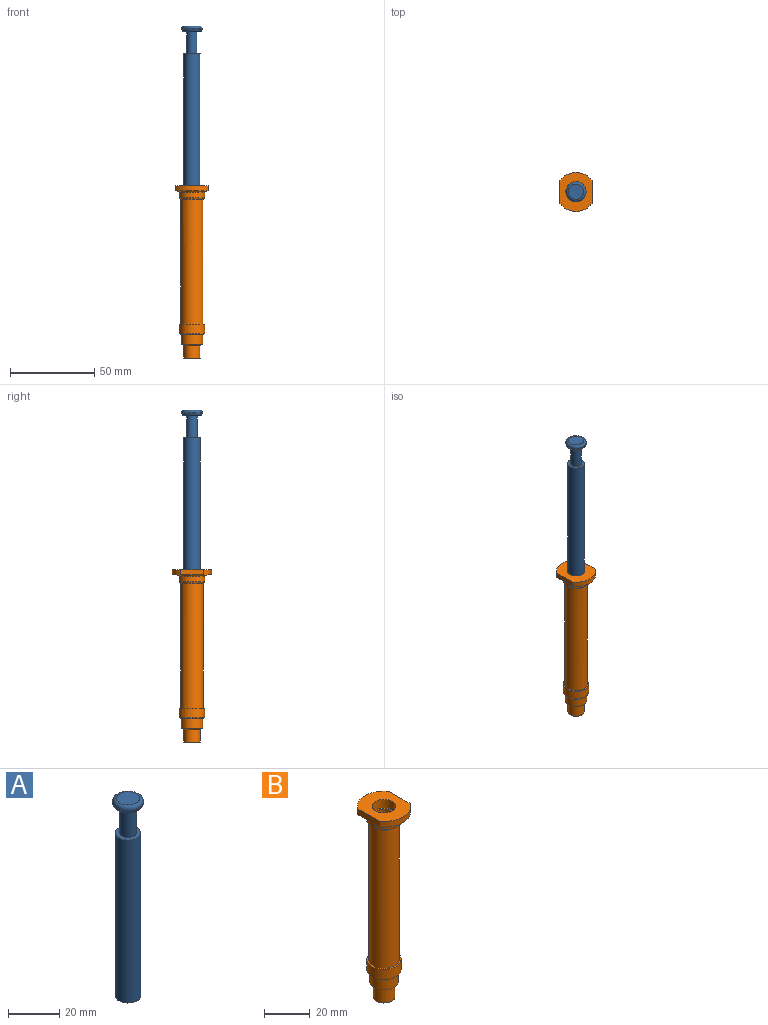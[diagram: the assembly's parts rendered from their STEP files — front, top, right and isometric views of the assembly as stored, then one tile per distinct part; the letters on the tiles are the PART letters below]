
ASSEMBLY  parts=2 mates=1
PART A: 9 faces, bbox 13x13x94.7 mm
  f0: plane 9.95x9.95mm, normal (0,0,-1), area 77.8mm2, adj f1
  f1: cylinder r=4.98mm len=78.2mm, axis (0,0,-1), area 2444.4mm2, adj f0,f2
  f2: plane 9.95x9.95mm, normal (0,0,1), area 44.6mm2, adj f1,f3
  f3: cylinder r=3.25mm len=13mm, axis (0,0,-1), area 265.5mm2, adj f2,f4
  f4: plane 9x9mm, normal (0,0,-1), area 30.4mm2, adj f3,f7
  f5: cylinder r=6mm len=12mm, axis (0,0,-1), area 18.8mm2, adj f7,f8
  f6: plane 9x9mm, normal (0,0,1), area 63.6mm2, adj f8
  f7: torus R=4.5mm, axis (0,0,-1), area 80.8mm2, adj f4,f5
  f8: torus R=4.5mm, axis (0,0,-1), area 80.8mm2, adj f5,f6
PART B: 29 faces, bbox 20.2x23.2x102.1 mm
  f0: cylinder r=11.58mm len=19mm, axis (0,0,-1), area 69.1mm2, adj f2,f3,f13,f14
  f1: cylinder r=11.58mm len=19mm, axis (0,0,-1), area 69.1mm2, adj f2,f3,f13,f14
  f2: plane 23.15x19mm, normal (0,0,-1), area 150.4mm2, adj f0,f1,f13,f14,f16
  f3: plane 23.15x19mm, normal (0,0,1), area 301.4mm2, adj f0,f1,f13,f14,f28
  f4: plane 9.55x9.55mm, normal (0,0,-1), area 71.6mm2, adj f5
  f5: cylinder r=4.77mm len=9.55mm, axis (0,0,-1), area 219mm2, adj f4,f6
  f6: plane 9.68x9.68mm, normal (0,0,-1), area 2mm2, adj f5,f18
  f7: cylinder r=6.34mm len=12.68mm, axis (0,0,-1), area 232.4mm2, adj f8,f18
  f8: plane 14.02x14.02mm, normal (0,0,-1), area 28.1mm2, adj f7,f17
  f9: cylinder r=7.51mm len=15.02mm, axis (0,0,-1), area 259.5mm2, adj f10,f17
  f10: plane 15.02x15.02mm, normal (0,0,1), area 34mm2, adj f9,f11
  f11: cylinder r=6.75mm len=74.01mm, axis (0,0,-1), area 3138.8mm2, adj f10,f15
  f12: cylinder r=7.62mm len=15.23mm, axis (0,0,-1), area 143.5mm2, adj f15,f16
  f13: plane 13.23x3.1mm, normal (1,0,0), area 41mm2, adj f0,f1,f2,f3
  f14: plane 13.23x3.1mm, normal (-1,0,0), area 41mm2, adj f0,f1,f2,f3
  f15: torus R=7.75mm, axis (0,0,1), area 63.7mm2, adj f11,f12
  f16: torus R=8.62mm, axis (0,0,-1), area 78.7mm2, adj f2,f12
  f17: cone r=7.01mm half-angle=45deg, axis (0,0,1), area 32.3mm2, adj f8,f9
  f18: cone r=4.84mm half-angle=60deg, axis (0,0,1), area 60.8mm2, adj f6,f7
  f19: plane 4.55x4.55mm, normal (0,0,1), area 16.3mm2, adj f20
  f20: cylinder r=2.27mm len=7.3mm, axis (0,0,-1), area 104.3mm2, adj f19,f21
  f21: plane 7.68x7.68mm, normal (0,0,1), area 30.1mm2, adj f20,f22
  f22: cylinder r=3.84mm len=7.68mm, axis (0,0,-1), area 161.7mm2, adj f21,f23
  f23: plane 10.02x10.02mm, normal (0,0,1), area 32.5mm2, adj f22,f24
  f24: cylinder r=5.01mm len=10.02mm, axis (0,0,-1), area 31.5mm2, adj f23,f25
  f25: plane 10.02x10.02mm, normal (0,0,-1), area 22.1mm2, adj f24,f26
  f26: cylinder r=4.25mm len=80mm, axis (0,0,-1), area 2136.3mm2, adj f25,f27
  f27: plane 10.23x10.23mm, normal (0,0,1), area 25.4mm2, adj f26,f28
  f28: cylinder r=5.11mm len=10.23mm, axis (0,0,-1), area 147.8mm2, adj f3,f27
PLACE A t=(-33.93,8.04,92.5)mm
PLACE B t=(-33.93,8.04,-9.6)mm fixed
MATE slider A.f1 <-> B.f0  axis (0,0,-1) through (-33.93,8.04,92.5)mm
